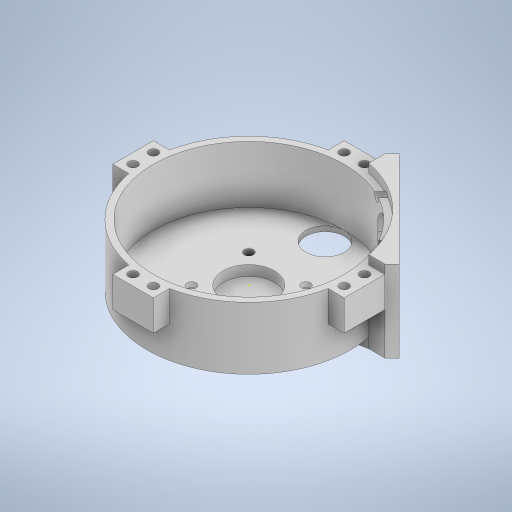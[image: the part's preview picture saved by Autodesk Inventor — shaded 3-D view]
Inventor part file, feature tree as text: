
AUTODESK INVENTOR PART (.ipt)
format: ipt  version: 2023 (Build 270158000, 158)  size: 524,288 bytes
history: native  units: in
note: dims shown in document units (in); Inventor stores cm internally (conversion verified against a paired STEP export)
features: sketch x19, extrude x15, hole x3
ambient origin geometry x8: Origin, YZ Plane, XZ Plane, XY Plane, X Axis, Y Axis, Z Axis, Center Point
bodies: Solid1 (feature_tree)
feature tree (37):
  extrude  "Extrusion1"  Depth=1.375in TaperAngle=0.0deg
  extrude  "Extrusion2"  Depth=1.275in TaperAngle=0.0deg
  extrude  "Extrusion3"  Depth=1.125in TaperAngle=0.0deg
  hole  "Hole1"  [1 undecoded]
  extrude  "Extrusion4"  Depth=0.4in
  extrude  "Extrusion5"  Depth=0.4in
  hole  "Hole2"  [1 undecoded]
  extrude  "Extrusion6"  Depth=0.4in
  sketch  "Sketch10"  dims[d26=0.8in d27=0.4in]
  extrude  "Extrusion7"  Depth=0.4in
  extrude  "Extrusion8"  Depth=0.8in
  extrude  "Extrusion9"  Depth=0.4in
  extrude  "Extrusion11"  Depth=0.75in TaperAngle=0.0deg
  extrude  "Extrusion12"  Depth=0.2in
  extrude  "Extrusion13"  Depth=0.2in
  extrude  "Extrusion14"  Depth=0.4in
  extrude  "Extrusion16"  Depth=0.2in
  hole  "Hole5"  [1 undecoded]
  extrude  "Extrusion17"  Depth=1.2in
  sketch  "Sketch1"  dims[d0=4.0in d1=1.375in d2=0.0in]
  sketch  "Sketch2"  dims[d3=3.75in d4=1.275in d5=0.0in]
  sketch  "Sketch3"  dims[d6=1.0in d7=1.125in d8=0.0in]
  sketch  "Sketch4"  dims[d9=1.125in d10=1.125in]
  sketch  "Sketch5"  dims[d11=0.177in d12=0.75in d13=0.332in d14=0.25in d15=0.5635in d16=1.0in d17=0.8108in d18=0.4in]
  sketch  "Sketch6"  dims[d19=0.4in d20=0.4in]
  sketch  "Sketch7"  dims[d21=0.4in d22=0.75in d23=0.0in]
  sketch  "Sketch8"  dims[d24=0.4in d25=0.4in]
  sketch  "Sketch11"  dims[d28=0.4in d29=0.8in]
  sketch  "Sketch12"  dims[d30=0.4in d31=0.4in]
  sketch  "Sketch13"  dims[d32=0.8in d33=0.75in d34=0.0in]
  sketch  "Sketch17"  dims[d35=0.2in d36=0.2in]
  sketch  "Sketch18"  dims[d37=0.4in d38=0.2in]
  sketch  "Sketch19"  dims[d39=0.2in d40=0.4in]
  sketch  "Sketch20"  dims[d41=0.2in d42=0.2in]
  sketch  "Sketch23"  dims[d43=0.2in d44=0.2in]
  sketch  "Sketch24"  dims[d45=0.4in]
  sketch  "Sketch25"  dims[d46=0.177in d47=0.75in d48=0.375in d49=0.25in d50=0.5635in d51=0.75in d52=0.8108in d53=1.5in d54=0.75in d55=0.0in d66=0.15in d67=0.0in d68=2.0in d69=0.275in d70=0.275in d71=0.275in d72=0.275in d73=0.1in d74=0.0in d75=0.1in d76=0.0in d79=0.175in d80=0.0in d81=0.2in d82=0.175in d83=0.0in d84=0.2in d85=0.0in d86=1.0875in d87=0.0in d101=1.425in d102=0.0in d103=1.425in d104=0.0in d105=0.3in d106=0.0in d107=0.8in d108=1.326in d109=1.18in d110=1.18in d111=0.169in d112=0.75in d113=0.375in d114=0.25in d115=0.5635in d116=0.75in d117=0.8108in d118=0.75in d119=1.2in d120=0.3in d121=0.0in]
note: 3 required parameter values undecoded (feature->parameter linkage not recoverable at this tier; creation-order binding heuristic only, values carry confidence <= 0.55)
